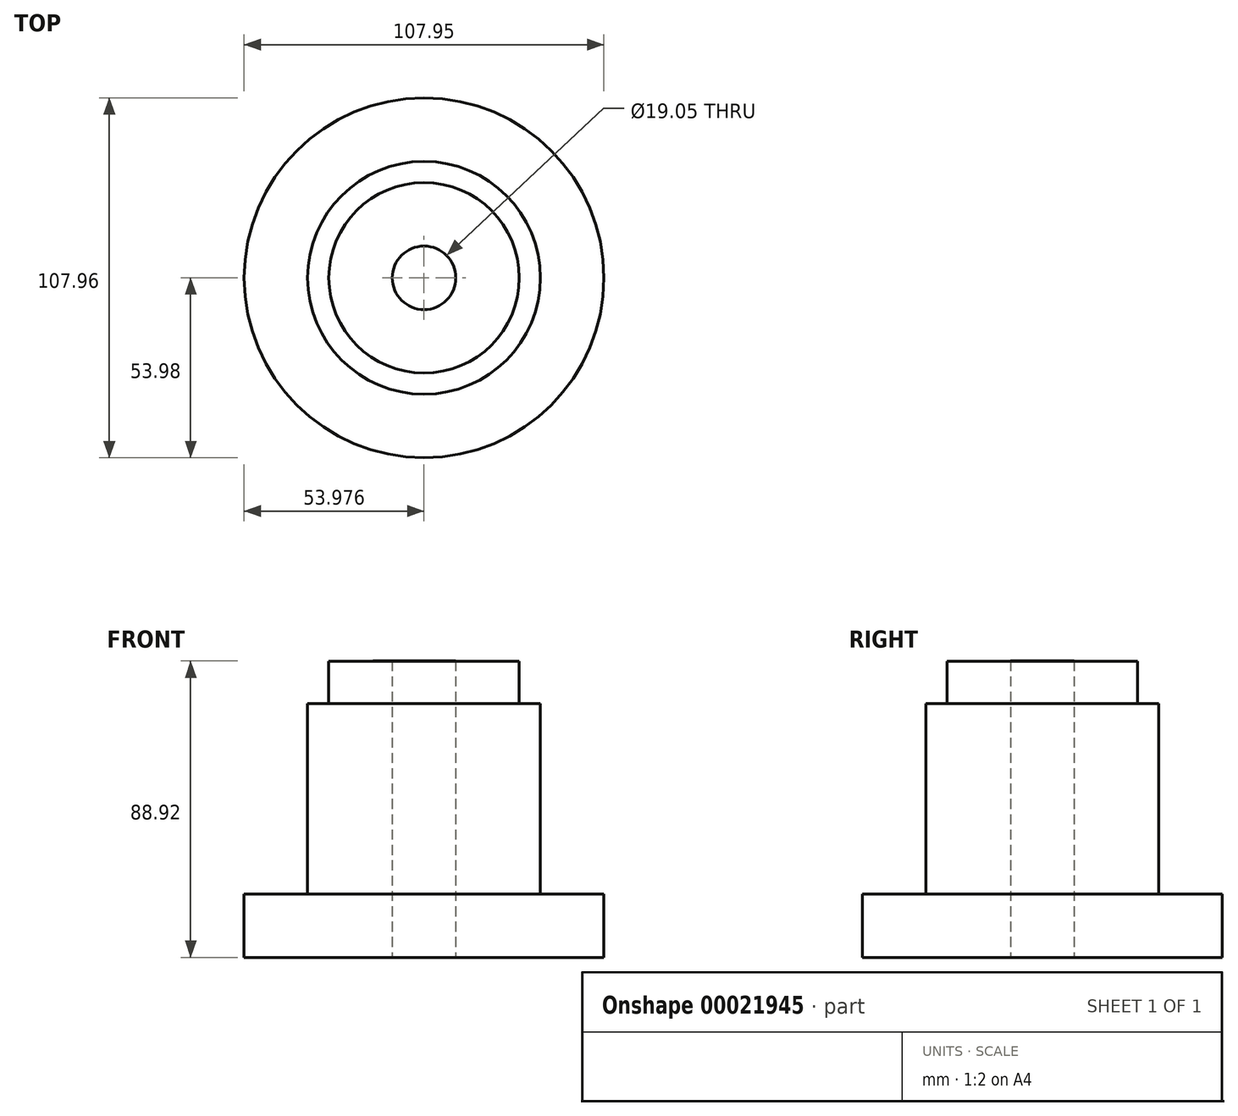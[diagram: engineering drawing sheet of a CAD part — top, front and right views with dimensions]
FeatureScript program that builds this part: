
annotation { "Feature Type Name" : "Feature", "Feature Type Description" : "" }
export const myFeature = defineFeature(function(context is Context, id is Id, definition is map)
    precondition{}
    {
        {
            var Q0;
            Q0=qCreatedBy(makeId("Front.planeOp"),FACE);
            var sketch = newSketch(context, id + "F0", { "sketchPlane" : qUnion([Q0])});
            skLineSegment(sketch, "E0", {"start": v(-0.34, -26.25) * mm, "end": v(44.11, -26.25) * mm});
            skLineSegment(sketch, "E1", {"start": v(44.11, -26.25) * mm, "end": v(44.11, -7.2) * mm});
            skLineSegment(sketch, "E2", {"start": v(44.11, -7.2) * mm, "end": v(25.06, -7.2) * mm});
            skLineSegment(sketch, "E3", {"start": v(25.06, -7.2) * mm, "end": v(25.06, 49.95) * mm});
            skLineSegment(sketch, "E4", {"start": v(25.06, 49.95) * mm, "end": v(18.71, 49.95) * mm});
            skLineSegment(sketch, "E5", {"start": v(18.71, 49.95) * mm, "end": v(18.71, 62.65) * mm});
            skLineSegment(sketch, "E6", {"start": v(-0.34, -26.25) * mm, "end": v(-0.34, 62.67) * mm});
            skLineSegment(sketch, "E7", {"start": v(18.71, 62.65) * mm, "end": v(-0.34, 62.67) * mm});
            skLineSegment(sketch, "E8", {"start": v(-9.86, -26.25) * mm, "end": v(-9.86, 30.76) * mm});
            skSolve(sketch);
        }
        {
            var Q0;
            Q0=makeQuery(id+"F0.imprint","IMPRINT",FACE,{"disambiguationData":[TD([[makeQuery(id+"F0.imprint","IMPRINT",EDGE,{"derivedFrom":sQuery(id+"F0.wireOp",EDGE,"E0")}),1.0]])]});
            var Q1;
            Q1=sQuery(id+"F0.wireOp",EDGE,"E8");
            revolve(context, id + "F1", {"entities" : qUnion([Q0]), "axis" : qUnion([Q1]), "revolveType" : RevolveType.FULL});
        }
    });
